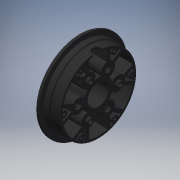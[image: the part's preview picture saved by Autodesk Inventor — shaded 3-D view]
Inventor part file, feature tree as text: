
AUTODESK INVENTOR PART (.ipt)
format: ipt  version: 2016 (Build 200138000, 138)  size: 951,296 bytes
history: native  units: in
note: dims shown in document units (in); Inventor stores cm internally (conversion verified against a paired STEP export)
features: fillet x1
ambient origin geometry x8: Origin, YZ Plane, XZ Plane, XY Plane, X Axis, Y Axis, Z Axis, Center Point
bodies: Solid1 (feature_tree)
feature tree (1):
  fillet  "Fillet7"  [1 undecoded]
note: 1 required parameter value undecoded (feature->parameter linkage not recoverable at this tier; creation-order binding heuristic only, values carry confidence <= 0.55)
